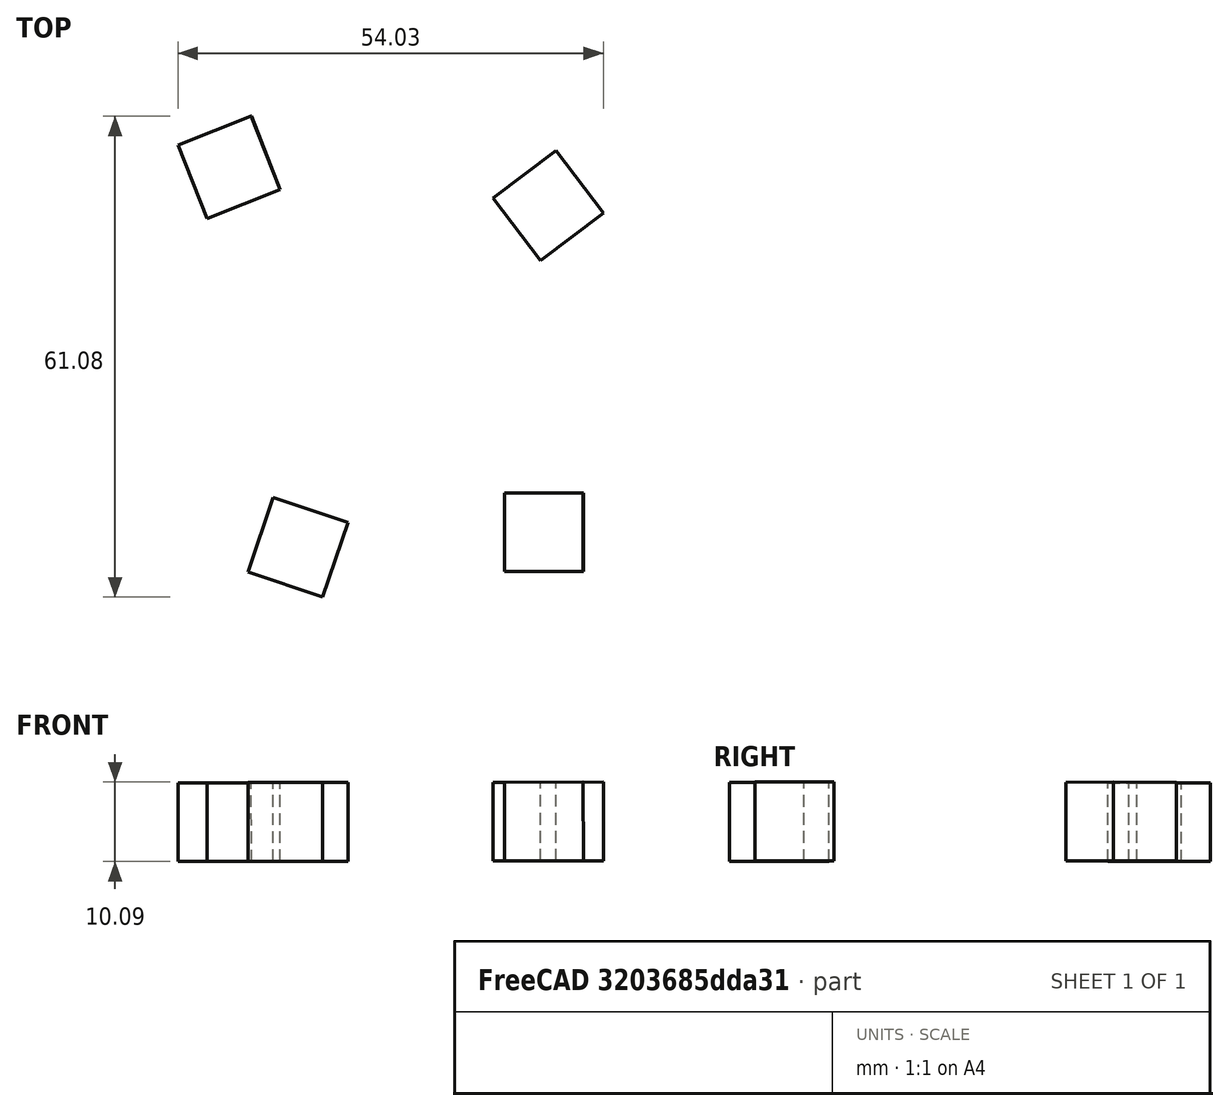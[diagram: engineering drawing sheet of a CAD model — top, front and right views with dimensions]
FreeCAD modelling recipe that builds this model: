
FCSTD DOCUMENT  (FreeCAD 0.16R6703 (Git))
Label: cajas-negras
License: All rights reserved
LicenseURL: http://en.wikipedia.org/wiki/All_rights_reserved
objects: Part::Box×4
note: 4 computed .brp shape members not serialized (recipe doc carries the construction recipe); baked Part::Feature solids carry a one-line shape summary decoded from their .brp

FEATURE [Part::Box] Box  label="Cube"
  Height = 10
  Length = 10
  Placement = pos=(-14.11,3.22311,4.12953e-06) rot=(0,0,-1;0.325946rad)
  Width = 10
FEATURE [Part::Box] Box001  label="Cube001"
  Height = 10
  Length = 10
  Placement = pos=(18.4773,3.28205,0.0307476) rot=(0,-1,0;0.001827rad)
  Width = 10
FEATURE [Part::Box] Box002  label="Cube002"
  Height = 10
  Length = 10
  Placement = pos=(23.0447,42.7686,0.0390921) rot=(-0.000913,-0.002725,0.999996;0.647014rad)
  Width = 10
FEATURE [Part::Box] Box003  label="Cube003"
  Height = 10
  Length = 10
  Placement = pos=(-19.3262,48.1346,-0.0378291) rot=(-0.000913,-0.00481,0.999988;0.375336rad)
  Width = 10
